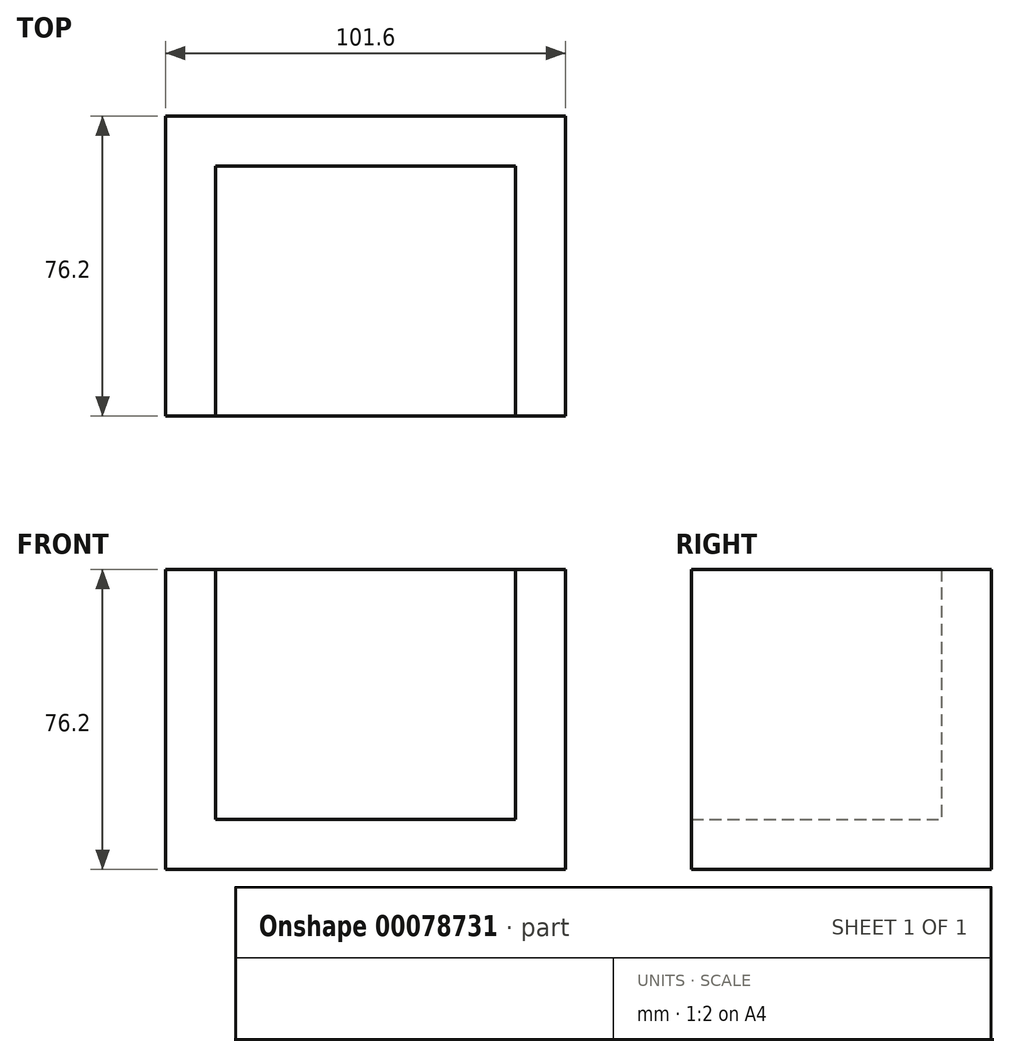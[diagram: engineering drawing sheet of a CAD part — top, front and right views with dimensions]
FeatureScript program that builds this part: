
annotation { "Feature Type Name" : "Feature", "Feature Type Description" : "" }
export const myFeature = defineFeature(function(context is Context, id is Id, definition is map)
    precondition{}
    {
        {
            var Q0;
            Q0=qCreatedBy(makeId("Front.planeOp"),FACE);
            var sketch = newSketch(context, id + "F0", { "sketchPlane" : qUnion([Q0])});
            skLineSegment(sketch, "E0.bottom", {"start": v(50.8, 38.1) * mm, "end": v(-50.8, 38.1) * mm});
            skLineSegment(sketch, "E0.top", {"start": v(50.8, -38.1) * mm, "end": v(-50.8, -38.1) * mm});
            skLineSegment(sketch, "E0.left", {"start": v(50.8, 38.1) * mm, "end": v(50.8, -38.1) * mm});
            skLineSegment(sketch, "E0.right", {"start": v(-50.8, 38.1) * mm, "end": v(-50.8, -38.1) * mm});
            skPoint(sketch, "E0.middle", {"position": v(0, 0) * mm});
            skSolve(sketch);
        }
        {
            var Q0;
            Q0 = qSketchRegion(id + "F0", true);
            extrude(context, id + "F1", {"entities" : qUnion([Q0]), "depth" : 50.8 * mm, "hasSecondDirection" : true, "secondDirectionOppositeDirection" : true, "secondDirectionDepth" : 50.8 * mm});
        }
        {
            var Q0;
            Q0=makeQuery(id+"F1.opExtrude","SWEPT_FACE",FACE,{"disambiguationData":[OSD([sQuery(id+"F0.wireOp",EDGE,"E0.bottom")])]});
            shell(context, id + "F2", {"entities" : qUnion([Q0]), "thickness" : 12.7 * mm});
        }
        {
            var Q0;
            Q0=makeQuery(id+"F1.opExtrude","CAP_FACE",FACE,{"disambiguationData":[OSD([sQuery(id+"F0.wireOp",EDGE,"E0.bottom"),sQuery(id+"F0.wireOp",EDGE,"E0.top"),sQuery(id+"F0.wireOp",EDGE,"E0.left"),sQuery(id+"F0.wireOp",EDGE,"E0.right")])],"isStart":false});
            extrude(context, id + "F3", {"entities" : qUnion([Q0]), "operationType" : NewBodyOperationType.REMOVE, "oppositeDirection" : true, "depth" : 25.4 * mm});
        }
    });
